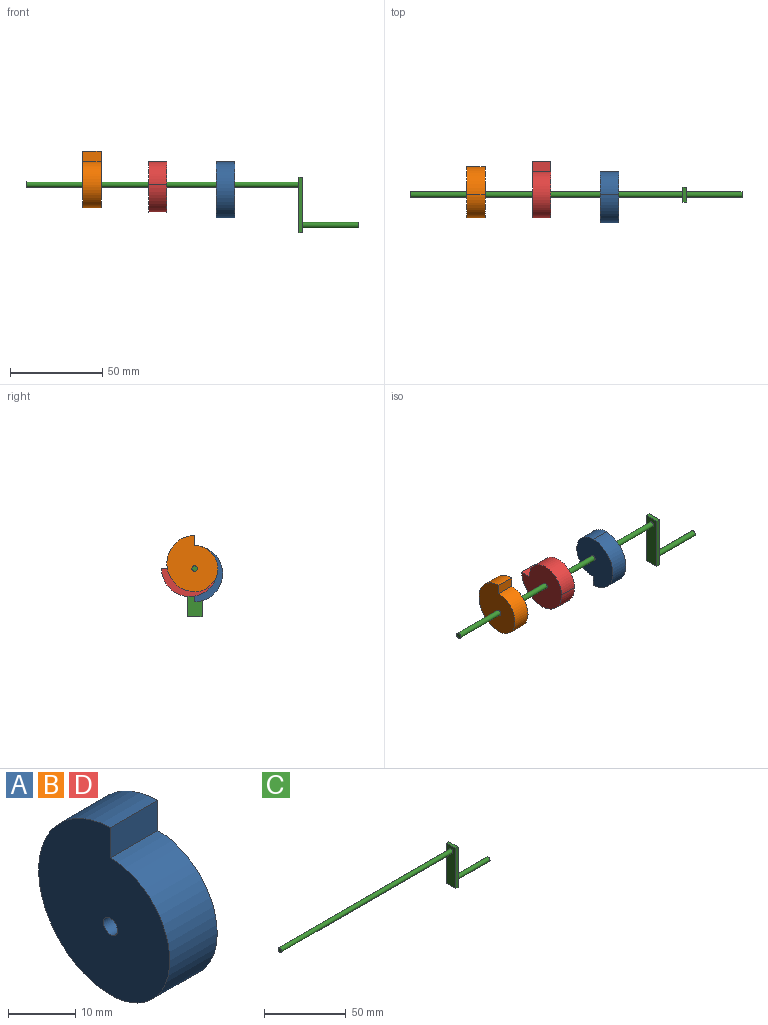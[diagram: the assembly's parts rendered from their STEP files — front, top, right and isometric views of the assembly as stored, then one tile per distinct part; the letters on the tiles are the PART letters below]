
ASSEMBLY  parts=4 mates=3
PART A: 6 faces, bbox 10x27.6x30.5 mm
  f0: cylinder r=12.5mm len=25mm, axis (-1,0,0), area 392.7mm2, adj f1,f3,f4,f5
  f1: cylinder r=15.25mm len=30.5mm, axis (-1,0,0), area 476.4mm2, adj f0,f3,f4,f5
  f2: cylinder r=1.5mm len=10mm, axis (-1,0,0), area 94.2mm2, adj f4,f5
  f3: plane 10x5.5mm, normal (0,-1,0), area 55mm2, adj f0,f1,f4,f5
  f4: plane 30.5x27.62mm, normal (1,0,0), area 599.6mm2, adj f0,f1,f2,f3
  f5: plane 30.5x27.62mm, normal (-1,0,0), area 599.6mm2, adj f0,f1,f2,f3
PART B: same geometry as A
PART C: 10 faces, bbox 180x8x30 mm
  f0: cylinder r=1.5mm len=148mm, axis (-1,0,0), area 1394.9mm2, adj f1,f6
  f1: plane 3x3mm, normal (-1,0,0), area 7.1mm2, adj f0
  f2: plane 30x2mm, normal (0,-1,0), area 60mm2, adj f3,f5,f6,f7
  f3: plane 8x2mm, normal (0,0,-1), area 16mm2, adj f2,f4,f6,f7
  f4: plane 30x2mm, normal (0,1,0), area 60mm2, adj f3,f5,f6,f7
  f5: plane 8x2mm, normal (0,0,1), area 16mm2, adj f2,f4,f6,f7
  f6: plane 30x8mm, normal (-1,0,0), area 232.9mm2, adj f0,f2,f3,f4,f5
  f7: plane 30x8mm, normal (1,0,0), area 232.9mm2, adj f2,f3,f4,f5,f8
  f8: cylinder r=1.5mm len=30mm, axis (-1,0,0), area 282.7mm2, adj f7,f9
  f9: plane 3x3mm, normal (1,0,0), area 7.1mm2, adj f8
PART D: same geometry as A
PLACE A rot(axis=(1,0,0),180deg) t=(103.16,0,0)mm
PLACE B t=(30.72,0,0)mm
PLACE C at identity
PLACE D rot(axis=(-1,0,0),90deg) t=(66.44,0,0)mm
MATE fastened A.f2 <-> C.f0  axis (-1,0,0) through (103.16,0,0)mm
MATE fastened B.f2 <-> C.f0  axis (-1,0,0) through (30.72,0,0)mm
MATE fastened D.f2 <-> C.f0  axis (-1,0,0) through (66.44,0,0)mm
